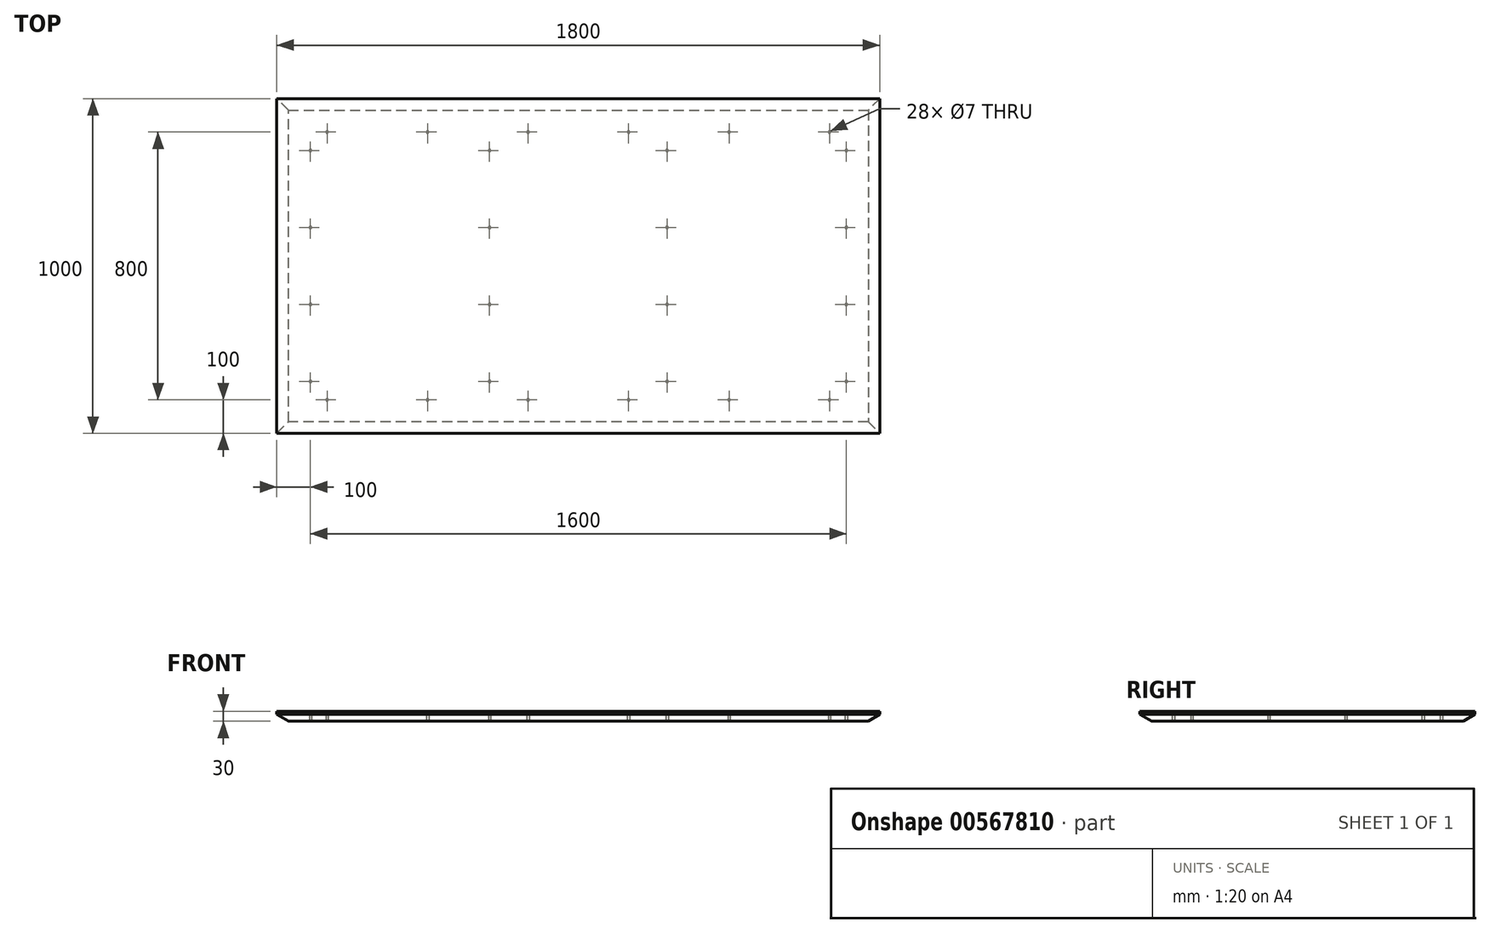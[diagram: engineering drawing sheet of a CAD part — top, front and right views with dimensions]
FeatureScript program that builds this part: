
annotation { "Feature Type Name" : "Feature", "Feature Type Description" : "" }
export const myFeature = defineFeature(function(context is Context, id is Id, definition is map)
    precondition{}
    {
        {
            var Q0;
            Q0=qCreatedBy(makeId("Top.planeOp"),FACE);
            var sketch = newSketch(context, id + "F0", { "sketchPlane" : qUnion([Q0])});
            skLineSegment(sketch, "E0.bottom", {"start": v(-900, 500) * mm, "end": v(900, 500) * mm});
            skLineSegment(sketch, "E0.top", {"start": v(-900, -500) * mm, "end": v(900, -500) * mm});
            skLineSegment(sketch, "E0.left", {"start": v(-900, 500) * mm, "end": v(-900, -500) * mm});
            skLineSegment(sketch, "E0.right", {"start": v(900, 500) * mm, "end": v(900, -500) * mm});
            skPoint(sketch, "E0.middle", {"position": v(0, 0) * mm});
            skSolve(sketch);
        }
        {
            var Q0;
            Q0=makeQuery(id+"F0.imprint","IMPRINT",FACE,{"disambiguationData":[TD([[makeQuery(id+"F0.imprint","IMPRINT",EDGE,{"derivedFrom":sQuery(id+"F0.wireOp",EDGE,"E0.bottom")}),-1.0]])]});
            extrude(context, id + "F1", {"entities" : qUnion([Q0]), "depth" : 10 * mm, "offsetDistance" : 25 * mm, "hasDraft" : true, "draftAngle" : 0 * degree, "hasSecondDirection" : true, "secondDirectionOppositeDirection" : true, "secondDirectionDepth" : 20 * mm, "hasSecondDirectionDraft" : true, "secondDirectionDraftAngle" : 60 * degree, "secondDirectionDraftPullDirection" : true});
        }
        {
            var Q0;
            Q0=makeQuery(id+"F1.opExtrude","CAP_FACE",FACE,{"disambiguationData":[OSD([sQuery(id+"F0.wireOp",EDGE,"E0.bottom"),sQuery(id+"F0.wireOp",EDGE,"E0.top"),sQuery(id+"F0.wireOp",EDGE,"E0.left"),sQuery(id+"F0.wireOp",EDGE,"E0.right")])],"isStart":true});
            var sketch = newSketch(context, id + "F2", { "sketchPlane" : qUnion([Q0])});
            skLineSegment(sketch, "E1.bottom", {"start": v(-800, 400) * mm, "end": v(800, 400) * mm});
            skLineSegment(sketch, "E1.top", {"start": v(-800, -400) * mm, "end": v(800, -400) * mm});
            skLineSegment(sketch, "E1.left", {"start": v(-800, 400) * mm, "end": v(-800, -400) * mm});
            skLineSegment(sketch, "E1.right", {"start": v(800, 400) * mm, "end": v(800, -400) * mm});
            skPoint(sketch, "E1.middle", {"position": v(0, 0) * mm});
            skPoint(sketch, "E2", {"position": v(-750, 400) * mm});
            skPoint(sketch, "E3", {"position": v(-450, 400) * mm});
            skPoint(sketch, "E4", {"position": v(-150, 400) * mm});
            skPoint(sketch, "E5", {"position": v(150, 400) * mm});
            skPoint(sketch, "E6", {"position": v(450, 400) * mm});
            skPoint(sketch, "E7", {"position": v(750, 400) * mm});
            skPoint(sketch, "E8", {"position": v(800, 345) * mm});
            skPoint(sketch, "E9", {"position": v(800, 115) * mm});
            skPoint(sketch, "E10", {"position": v(800, -115) * mm});
            skPoint(sketch, "E11", {"position": v(800, -345) * mm});
            skPoint(sketch, "E12", {"position": v(750, -400) * mm});
            skPoint(sketch, "E13", {"position": v(450, -400) * mm});
            skPoint(sketch, "E14", {"position": v(150, -400) * mm});
            skPoint(sketch, "E15", {"position": v(-150, -400) * mm});
            skPoint(sketch, "E16", {"position": v(-450, -400) * mm});
            skPoint(sketch, "E17", {"position": v(-750, -400) * mm});
            skPoint(sketch, "E18", {"position": v(-800, -345) * mm});
            skPoint(sketch, "E19", {"position": v(-800, -115) * mm});
            skPoint(sketch, "E20", {"position": v(-800, 115) * mm});
            skPoint(sketch, "E21", {"position": v(-800, 345) * mm});
            skLineSegment(sketch, "E22", {"start": v(-265, 400) * mm, "end": v(-265, -400) * mm});
            skLineSegment(sketch, "E23", {"start": v(265, 400) * mm, "end": v(265, -400) * mm});
            skPoint(sketch, "E24", {"position": v(-265, 345) * mm});
            skPoint(sketch, "E25", {"position": v(-265, 115) * mm});
            skPoint(sketch, "E26", {"position": v(-265, -115) * mm});
            skPoint(sketch, "E27", {"position": v(-265, -345) * mm});
            skPoint(sketch, "E28", {"position": v(265, -345) * mm});
            skPoint(sketch, "E29", {"position": v(265, -115) * mm});
            skPoint(sketch, "E30", {"position": v(265, 115) * mm});
            skPoint(sketch, "E31", {"position": v(265, 345) * mm});
            skSolve(sketch);
        }
        {
            var Q0;
            Q0=sQuery(id+"F2.wireOp",VERTEX,"E11");
            var Q1;
            Q1=sQuery(id+"F2.wireOp",VERTEX,"E10");
            var Q2;
            Q2=sQuery(id+"F2.wireOp",VERTEX,"E9");
            var Q3;
            Q3=sQuery(id+"F2.wireOp",VERTEX,"E8");
            var Q4;
            Q4=sQuery(id+"F2.wireOp",VERTEX,"E7");
            var Q5;
            Q5=sQuery(id+"F2.wireOp",VERTEX,"E6");
            var Q6;
            Q6=sQuery(id+"F2.wireOp",VERTEX,"E5");
            var Q7;
            Q7=sQuery(id+"F2.wireOp",VERTEX,"E4");
            var Q8;
            Q8=sQuery(id+"F2.wireOp",VERTEX,"E3");
            var Q9;
            Q9=sQuery(id+"F2.wireOp",VERTEX,"E2");
            var Q10;
            Q10=sQuery(id+"F2.wireOp",VERTEX,"E13");
            var Q11;
            Q11=sQuery(id+"F2.wireOp",VERTEX,"E14");
            var Q12;
            Q12=sQuery(id+"F2.wireOp",VERTEX,"E15");
            var Q13;
            Q13=sQuery(id+"F2.wireOp",VERTEX,"E15");
            var Q14;
            Q14=sQuery(id+"F2.wireOp",VERTEX,"E18");
            var Q15;
            Q15=sQuery(id+"F2.wireOp",VERTEX,"E19");
            var Q16;
            Q16=sQuery(id+"F2.wireOp",VERTEX,"E20");
            var Q17;
            Q17=sQuery(id+"F2.wireOp",VERTEX,"E16");
            var Q18;
            Q18=sQuery(id+"F2.wireOp",VERTEX,"E17");
            var Q19;
            Q19=sQuery(id+"F2.wireOp",VERTEX,"E12");
            var Q20;
            Q20=sQuery(id+"F2.wireOp",VERTEX,"E21");
            var Q21;
            Q21=sQuery(id+"F2.wireOp",VERTEX,"E24");
            var Q22;
            Q22=sQuery(id+"F2.wireOp",VERTEX,"E25");
            var Q23;
            Q23=sQuery(id+"F2.wireOp",VERTEX,"E26");
            var Q24;
            Q24=sQuery(id+"F2.wireOp",VERTEX,"E27");
            var Q25;
            Q25=sQuery(id+"F2.wireOp",VERTEX,"E28");
            var Q26;
            Q26=sQuery(id+"F2.wireOp",VERTEX,"E28");
            var Q27;
            Q27=sQuery(id+"F2.wireOp",VERTEX,"E29");
            var Q28;
            Q28=sQuery(id+"F2.wireOp",VERTEX,"E31");
            var Q29;
            Q29=sQuery(id+"F2.wireOp",VERTEX,"E30");
            var Q30;
            Q30=makeQuery(id+"F1.*.split.splitOp","SPLIT",BODY,{"derivedFrom":makeQuery(id+"F1.opExtrude","SWEPT_BODY",BODY,{"disambiguationData":[OSD([sQuery(id+"F0.wireOp",EDGE,"E0.bottom"),sQuery(id+"F0.wireOp",EDGE,"E0.top"),sQuery(id+"F0.wireOp",EDGE,"E0.left"),sQuery(id+"F0.wireOp",EDGE,"E0.right")])]})});
            hole(context, id + "F3", {"style" : HoleStyle.SIMPLE, "endStyle" : HoleEndStyle.BLIND, "holeDiameter" : 7 * mm, "holeDepth" : 20 * mm, "isTappedThrough" : true, "tappedDepth" : 12 * mm, "tapClearance" : 3, "locations" : qUnion([Q0, Q1, Q2, Q3, Q4, Q5, Q6, Q7, Q8, Q9, Q10, Q11, Q12, Q13, Q14, Q15, Q16, Q17, Q18, Q19, Q20, Q21, Q22, Q23, Q24, Q25, Q26, Q27, Q28, Q29]), "scope" : qUnion([Q30]), "majorDiameter" : 5 * mm});
        }
    });
